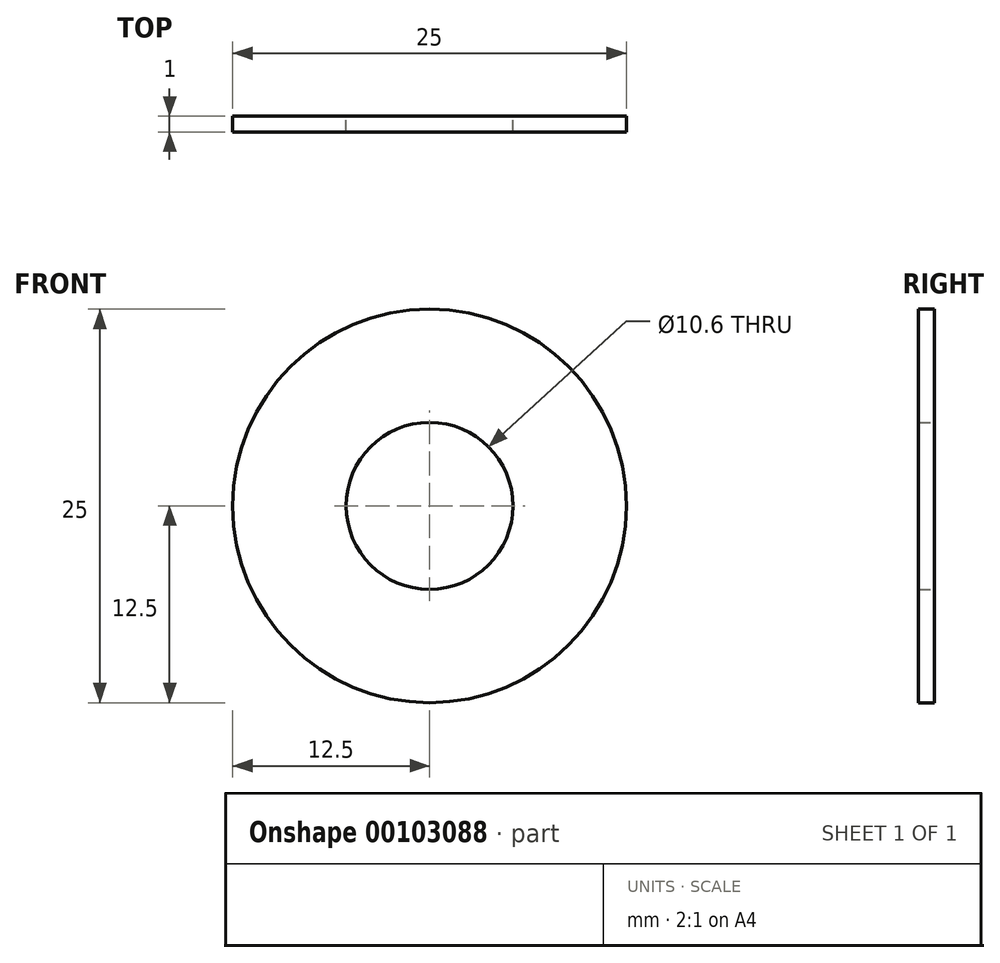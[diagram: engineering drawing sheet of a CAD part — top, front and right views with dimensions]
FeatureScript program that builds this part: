
annotation { "Feature Type Name" : "Feature", "Feature Type Description" : "" }
export const myFeature = defineFeature(function(context is Context, id is Id, definition is map)
    precondition{}
    {
        {
            var Q0;
            Q0=qCreatedBy(makeId("Front.planeOp"),FACE);
            var sketch = newSketch(context, id + "F0", { "sketchPlane" : qUnion([Q0])});
            skCircle(sketch, "E0", {"center": v(0, 0) * mm, "radius": 12.5 * mm});
            skCircle(sketch, "E1", {"center": v(0, 0) * mm, "radius": 5.3 * mm});
            skSolve(sketch);
        }
        {
            var Q0;
            Q0 = qSketchRegion(id + "F0", true);
            extrude(context, id + "F1", {"entities" : qUnion([Q0]), "depth" : 1 * mm});
        }
    });
